# Revit family: Access_Flooring-FreeAxez-Ramp_Internal-1_20
name_source: partatom
category: Specialty Equipment
units: mm (PartAtom-declared; Revit-internal decimal feet)

## family parameters
Always vertical = Yes
Cut with Voids When Loaded = No
Enable Cutting in Views = No
Maintain Annotation Orientation = No
OmniClass Number = 23.35.50.27.14
OmniClass Title = Rigid Grid Access Flooring
Part Type = Normal
Room Calculation Point = No
Round Connector Dimension = Use Diameter
Shared = No
Work Plane-Based = No

## types (2) — shared parameters
Default Elevation = 0' - 0"
Manufacturer = FreeAxez
Product Documentation Link = https://www.freeaxez.com
Product Page URL = https://www.freeaxez.com
URL = https://www.freeaxez.com
zero-valued in all types: Cost

## per-type parameters (varying)
| type | Description | Height | Model | Width |
| Gridd40 | Gridd40 Ramp Internal 1:20 | 0' - 1 9/16" | FA-4433in | 2' - 9" |
| Gridd70 | Gridd70 Ramp Internal 1:20 | 0' - 2 3/4" | FA-7455in | 4' - 7" |

## geometry (parser evidence)
native form markers: Sweep x3
no freeform markers — native parametric forms only
